# Revit family: Reece_Accessory_Kado_Lux_3 in 1 Heat Lamp, Exhaust Fan and LED
name_source: partatom
category: Mechanical Equipment
revit_build: Autodesk Revit 2018 (Build: 20190510_1515(x64)
units: mm (PartAtom-declared; Revit-internal decimal feet)

## family parameters
Classification = None
Cut with Voids When Loaded = No
Host = Face
Part Type = Normal
Room Calculation Point = Yes
Round Connector Dimension = Use Diameter
Shared = Yes

## types (1)
- 530 mm x 360 mm_White
    Default Elevation = 0 mm  [stored 0 ft]
    Description = Kado Lux 3-in-1 Heat Lamp Exhaust White
    Disclaimer = THIS FILE IS THE PROPERTY OF THE REECE GROUP. IT MAY NOT BE REPRODUCED, REVERSE-ENGINEERED OR MODIFIED. ANY REPUBLICATION, TRANSMISSION OR DISTRIBUTION FOR THE PURPOSE OF COMMERCIALLY EXPLOITING THE FILES IS PROHIBITED.
    Keynote = Product #2053301, Reece_Accessory_Kado_Lux_3 in 1 Heat Lamp, Exhaust Fan and LED - 530 mm x 360 mm_White
    Manufacturer = Kado
    Model = Lux
    Reece_Ceiling_Cutout_Length = 330 mm  [stored 1.08268 ft]
    Reece_Ceiling_Cutout_Width = 505 mm  [stored 1.65682 ft]
    Reece_Detail_Connector = Hardwired
    Reece_Detail_Disclaimer = THIS FILE IS THE PROPERTY OF THE REECE GROUP. IT MAY NOT BE REPRODUCED, REVERSE-ENGINEERED OR MODIFIED. ANY REPUBLICATION, TRANSMISSION OR DISTRIBUTION FOR THE PURPOSE OF COMMERCIALLY EXPLOITING THE FILES IS PROHIBITED.
    Reece_Detail_Installation = 3 in 1 Heater, Exhaust Fan and LED
    Reece_Detail_Note = Electrical input required. Refer to web page for further details.
    Reece_Electrical_Fan Power_Wattage = 65 W
    Reece_Electrical_Frequency = 50 Hz
    Reece_Electrical_Heat_Wattage = 800 W
    Reece_Electrical_IP Rating = IPX4
    Reece_Electrical_LED Light_Wattage = 18 W
    Reece_Electrical_Voltage = 240 V
    Reece_Electrical_Voltage_Max = 240 V
    Reece_Electrical_Voltage_Min = 220 V
    Reece_Equipment_Weight = 7.86 kg
    Reece_Installation_Minimum Depth = 220 mm  [stored 0.721785 ft]
    Reece_Material-Main = Reece_Metal_White
    Reece_Material_Base = Reece_Glass_Frosted
    Reece_Material_Colour = Reece_Plastic_Frosted
    Reece_Material_Secondary = Reece_Metal_Galvanised
    Reece_Mechanical_Duct_Diameter = 150 mm
    Reece_Mechanical_Max Airflow = 330 m³/h
    Reece_Overall_Length = 360 mm  [stored 1.1811 ft]
    Reece_Overall_Width = 530 mm  [stored 1.73885 ft]
    Reece_Product_Brand = Kado
    Reece_Product_Description = Kado Lux 3-in-1 Heat Lamp Exhaust White
    Reece_Product_Mount = Ceiling Mounted
    Reece_Product_Number = 2053301
    Reece_Product_Sub Brand = Lux
    Reece_Product_Type = Accessory
    Reece_Product_Web Page = https://www.reece.com.au
    Type Comments = Accessory
    URL = https://www.reece.com.au

note: [stored X ft] marks values corroborated as IEEE doubles in the binary element streams (Revit-internal decimal feet)

## geometry (parser evidence)
native form markers: Sweep x6
no freeform markers — native parametric forms only
